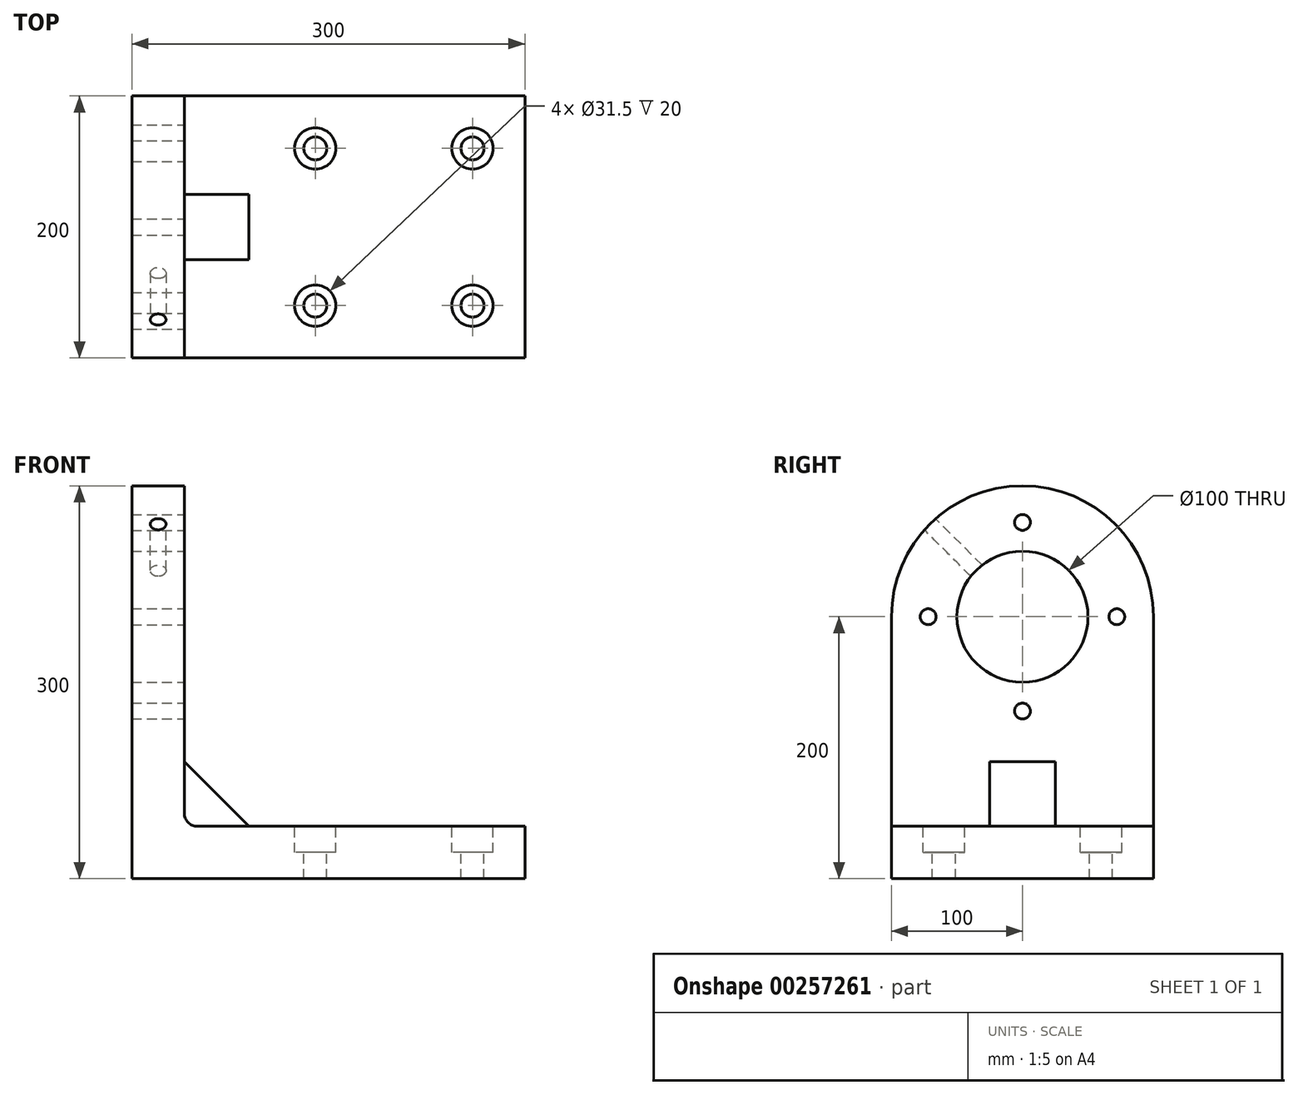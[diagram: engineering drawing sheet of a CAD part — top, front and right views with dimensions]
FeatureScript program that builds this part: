
annotation { "Feature Type Name" : "Feature", "Feature Type Description" : "" }
export const myFeature = defineFeature(function(context is Context, id is Id, definition is map)
    precondition{}
    {
        {
            var Q0;
            Q0=qCreatedBy(makeId("Front.planeOp"),FACE);
            var sketch = newSketch(context, id + "F0", { "sketchPlane" : qUnion([Q0])});
            skLineSegment(sketch, "E0", {"start": v(227.77, 0) * mm, "end": v(-72.23, 0) * mm});
            skLineSegment(sketch, "E1", {"start": v(-72.23, 0) * mm, "end": v(-72.23, 300) * mm});
            skLineSegment(sketch, "E2", {"start": v(-72.23, 300) * mm, "end": v(-32.23, 300) * mm});
            skLineSegment(sketch, "E3", {"start": v(-32.23, 300) * mm, "end": v(-32.23, 40) * mm});
            skLineSegment(sketch, "E4", {"start": v(-32.23, 40) * mm, "end": v(227.77, 40) * mm});
            skLineSegment(sketch, "E5", {"start": v(227.77, 40) * mm, "end": v(227.77, 0) * mm});
            skSolve(sketch);
        }
        {
            var Q0;
            Q0=makeQuery(id+"F0.imprint","IMPRINT",FACE,{"disambiguationData":[TD([[makeQuery(id+"F0.imprint","IMPRINT",EDGE,{"derivedFrom":sQuery(id+"F0.wireOp",EDGE,"E0")}),-1.0]])]});
            extrude(context, id + "F1", {"entities" : qUnion([Q0]), "endBound" : BoundingType.SYMMETRIC, "depth" : 200 * mm});
        }
        {
            var Q0;
            Q0=makeQuery(id+"F1.opExtrude","CAP_EDGE",EDGE,{"disambiguationData":[OSD([sQuery(id+"F0.wireOp",EDGE,"E2")])],"isStart":false});
            var Q1;
            Q1=makeQuery(id+"F1.opExtrude","CAP_EDGE",EDGE,{"disambiguationData":[OSD([sQuery(id+"F0.wireOp",EDGE,"E2")])],"isStart":true});
            fillet(context, id + "F2", {"entities" : qUnion([Q0, Q1]), "radius" : 100 * mm, "tangentPropagation" : true, "allowEdgeOverflow" : false});
        }
        {
            var Q0;
            Q0=makeQuery(id+"F1.opExtrude","SWEPT_FACE",FACE,{"disambiguationData":[OSD([sQuery(id+"F0.wireOp",EDGE,"E4")])]});
            var sketch = newSketch(context, id + "F3", { "sketchPlane" : qUnion([Q0])});
            skCircle(sketch, "E6", {"center": v(187.77, 60) * mm, "radius": 8.75 * mm});
            skCircle(sketch, "E7", {"center": v(67.77, 60) * mm, "radius": 8.75 * mm});
            skCircle(sketch, "E8", {"center": v(67.77, -60) * mm, "radius": 8.75 * mm});
            skCircle(sketch, "E9", {"center": v(187.77, -60) * mm, "radius": 8.75 * mm});
            skCircle(sketch, "E10", {"center": v(67.77, 60) * mm, "radius": 15.75 * mm});
            skCircle(sketch, "E11", {"center": v(187.77, 60) * mm, "radius": 15.75 * mm});
            skCircle(sketch, "E12", {"center": v(187.77, -60) * mm, "radius": 15.75 * mm});
            skCircle(sketch, "E13", {"center": v(67.77, -60) * mm, "radius": 15.75 * mm});
            skSolve(sketch);
        }
        {
            var Q0;
            Q0=makeQuery(id+"F3.imprint","IMPRINT",FACE,{"disambiguationData":[TD([[makeQuery(id+"F3.imprint","IMPRINT",EDGE,{"derivedFrom":sQuery(id+"F3.wireOp",EDGE,"E7")}),1.0]])]});
            var Q1;
            Q1=makeQuery(id+"F3.imprint","IMPRINT",FACE,{"disambiguationData":[TD([[makeQuery(id+"F3.imprint","IMPRINT",EDGE,{"derivedFrom":sQuery(id+"F3.wireOp",EDGE,"E6")}),1.0]])]});
            var Q2;
            Q2=makeQuery(id+"F3.imprint","IMPRINT",FACE,{"disambiguationData":[TD([[makeQuery(id+"F3.imprint","IMPRINT",EDGE,{"derivedFrom":sQuery(id+"F3.wireOp",EDGE,"E8")}),1.0]])]});
            var Q3;
            Q3=makeQuery(id+"F3.imprint","IMPRINT",FACE,{"disambiguationData":[TD([[makeQuery(id+"F3.imprint","IMPRINT",EDGE,{"derivedFrom":sQuery(id+"F3.wireOp",EDGE,"E9")}),1.0]])]});
            extrude(context, id + "F4", {"entities" : qUnion([Q0, Q1, Q2, Q3]), "operationType" : NewBodyOperationType.REMOVE, "endBound" : BoundingType.THROUGH_ALL, "oppositeDirection" : true, "depth" : 25.4 * mm});
        }
        {
            var Q0;
            Q0=makeQuery(id+"F3.imprint","IMPRINT",FACE,{"disambiguationData":[TD([[makeQuery(id+"F3.imprint","IMPRINT",EDGE,{"derivedFrom":sQuery(id+"F3.wireOp",EDGE,"E6")}),-1.0]])]});
            var Q1;
            Q1=makeQuery(id+"F3.imprint","IMPRINT",FACE,{"disambiguationData":[TD([[makeQuery(id+"F3.imprint","IMPRINT",EDGE,{"derivedFrom":sQuery(id+"F3.wireOp",EDGE,"E7")}),-1.0]])]});
            var Q2;
            Q2=makeQuery(id+"F3.imprint","IMPRINT",FACE,{"disambiguationData":[TD([[makeQuery(id+"F3.imprint","IMPRINT",EDGE,{"derivedFrom":sQuery(id+"F3.wireOp",EDGE,"E8")}),-1.0]])]});
            var Q3;
            Q3=makeQuery(id+"F3.imprint","IMPRINT",FACE,{"disambiguationData":[TD([[makeQuery(id+"F3.imprint","IMPRINT",EDGE,{"derivedFrom":sQuery(id+"F3.wireOp",EDGE,"E9")}),-1.0]])]});
            extrude(context, id + "F5", {"entities" : qUnion([Q0, Q1, Q2, Q3]), "operationType" : NewBodyOperationType.REMOVE, "oppositeDirection" : true, "depth" : 20 * mm});
        }
        {
            var Q0;
            Q0=makeQuery(id+"F1.opExtrude","SWEPT_FACE",FACE,{"disambiguationData":[OSD([sQuery(id+"F0.wireOp",EDGE,"E3")])]});
            var sketch = newSketch(context, id + "F6", { "sketchPlane" : qUnion([Q0])});
            skCircle(sketch, "E14", {"center": v(0, 200) * mm, "radius": 50 * mm});
            skSolve(sketch);
        }
        {
            var Q0;
            Q0=makeQuery(id+"F6.imprint","IMPRINT",FACE,{"disambiguationData":[TD([[makeQuery(id+"F6.imprint","IMPRINT",EDGE,{"derivedFrom":sQuery(id+"F6.wireOp",EDGE,"E14")}),1.0]])]});
            extrude(context, id + "F7", {"entities" : qUnion([Q0]), "operationType" : NewBodyOperationType.REMOVE, "endBound" : BoundingType.THROUGH_ALL, "oppositeDirection" : true, "depth" : 25.4 * mm});
        }
        {
            var Q0;
            Q0=makeQuery(id+"F6.imprint","IMPRINT",FACE,{"disambiguationData":[TD([[makeQuery(id+"F6.imprint","IMPRINT",EDGE,{"derivedFrom":sQuery(id+"F6.wireOp",EDGE,"E14")}),-1.0]])]});
            var sketch = newSketch(context, id + "F8", { "sketchPlane" : qUnion([Q0])});
            skCircle(sketch, "E15", {"center": v(0, 200) * mm, "radius": 72 * mm, "construction": true});
            skPoint(sketch, "E16", {"position": v(72, 200) * mm});
            skPoint(sketch, "E17", {"position": v(0, 272) * mm});
            skPoint(sketch, "E18", {"position": v(-72, 200) * mm});
            skPoint(sketch, "E19", {"position": v(0, 128) * mm});
            skLineSegment(sketch, "E20", {"start": v(0, 200) * mm, "end": v(-70.71, 270.71) * mm, "construction": true});
            skLineSegment(sketch, "E21", {"start": v(0, 200) * mm, "end": v(0, 272) * mm, "construction": true});
            skSolve(sketch);
        }
        {
            var Q0;
            Q0=makeQuery(id+"F1.opExtrude","CAP_FACE",FACE,{"disambiguationData":[OSD([sQuery(id+"F0.wireOp",EDGE,"E0"),sQuery(id+"F0.wireOp",EDGE,"E1"),sQuery(id+"F0.wireOp",EDGE,"E2"),sQuery(id+"F0.wireOp",EDGE,"E3"),sQuery(id+"F0.wireOp",EDGE,"E4"),sQuery(id+"F0.wireOp",EDGE,"E5")])],"isStart":true});
            cPlane(context, id + "F9", {"entities" : qUnion([Q0]), "cplaneType" : CPlaneType.OFFSET, "offset" : 100 * mm, "oppositeDirection" : true, "width" : 152.4 * mm, "height" : 152.4 * mm});
        }
        {
            var Q0;
            Q0=qCreatedBy(id+"F9.planeOp",FACE);
            var sketch = newSketch(context, id + "F10", { "sketchPlane" : qUnion([Q0])});
            skLineSegment(sketch, "E22.0", {"start": v(32.23, 40) * mm, "end": v(-227.77, 40) * mm});
            skLineSegment(sketch, "E23.0", {"start": v(32.23, 200) * mm, "end": v(32.23, 40) * mm});
            skLineSegment(sketch, "E24", {"start": v(-17.15, 40) * mm, "end": v(32.23, 89.38) * mm});
            skSolve(sketch);
        }
        {
            var Q0;
            Q0 = qSketchRegion(id + "F10", true);
            extrude(context, id + "F11", {"entities" : qUnion([Q0]), "operationType" : NewBodyOperationType.ADD, "endBound" : BoundingType.SYMMETRIC, "depth" : 50 * mm});
        }
        {
            var Q0;
            {var subQ0=sQuery(id+"F0.wireOp",EDGE,"E4");var subQ1=sQuery(id+"F0.wireOp",EDGE,"E3");Q0=makeQuery(id+"F11.boolean.opBoolean","SPLIT",EDGE,{"disambiguationData":[TD([makeQuery(id+"F11.opExtrude","CAP_FACE",FACE,{"disambiguationData":[OSD([sQuery(id+"F10.wireOp",EDGE,"E22.0"),sQuery(id+"F10.wireOp",EDGE,"E23.0"),sQuery(id+"F10.wireOp",EDGE,"E24")])],"isStart":false})])],"derivedFrom":makeQuery(id+"F1.opExtrude","SWEPT_EDGE",EDGE,{"disambiguationData":[OSD([subQ1,subQ0])]})});}
            var Q1;
            {var subQ0=sQuery(id+"F0.wireOp",EDGE,"E4");var subQ1=sQuery(id+"F0.wireOp",EDGE,"E3");Q1=makeQuery(id+"F11.boolean.opBoolean","SPLIT",EDGE,{"disambiguationData":[TD([makeQuery(id+"F11.opExtrude","CAP_FACE",FACE,{"disambiguationData":[OSD([sQuery(id+"F10.wireOp",EDGE,"E22.0"),sQuery(id+"F10.wireOp",EDGE,"E23.0"),sQuery(id+"F10.wireOp",EDGE,"E24")])],"isStart":true})])],"derivedFrom":makeQuery(id+"F1.opExtrude","SWEPT_EDGE",EDGE,{"disambiguationData":[OSD([subQ1,subQ0])]})});}
            fillet(context, id + "F12", {"entities" : qUnion([Q0, Q1]), "radius" : 10 * mm, "tangentPropagation" : true, "allowEdgeOverflow" : false});
        }
        {
            var Q0;
            Q0=sQuery(id+"F8.wireOp",VERTEX,"E17");
            var Q1;
            Q1=sQuery(id+"F8.wireOp",VERTEX,"E16");
            var Q2;
            Q2=sQuery(id+"F8.wireOp",VERTEX,"E19");
            var Q3;
            Q3=sQuery(id+"F8.wireOp",VERTEX,"E18");
            var Q4;
            Q4=makeQuery(id+"F1.opExtrude","SWEPT_BODY",BODY,{"disambiguationData":[OSD([sQuery(id+"F0.wireOp",EDGE,"E0"),sQuery(id+"F0.wireOp",EDGE,"E1"),sQuery(id+"F0.wireOp",EDGE,"E2"),sQuery(id+"F0.wireOp",EDGE,"E3"),sQuery(id+"F0.wireOp",EDGE,"E4"),sQuery(id+"F0.wireOp",EDGE,"E5")])]});
            hole(context, id + "F13", {"style" : HoleStyle.SIMPLE, "endStyle" : HoleEndStyle.THROUGH, "standardTappedOrClearance" : lookupTablePath({ "standard" : "ISO", "engagement" : "75%", "pitch" : "2 mm", "size" : "M14", "type" : "Tapped" }), "standardBlindInLast" : lookupTablePath({ "standard" : "ISO", "engagement" : "75%", "pitch" : "2 mm", "size" : "M14", "type" : "Tapped" }), "holeDiameter" : 12.1 * mm, "showTappedDepth" : true, "tappedDepth" : 12.7 * mm, "tapClearance" : 3, "locations" : qUnion([Q0, Q1, Q2, Q3]), "scope" : qUnion([Q4]), "majorDiameter" : 14 * mm});
        }
        {
            var Q0;
            Q0=sQuery(id+"F8.wireOp",EDGE,"E20");
            var Q1;
            Q1=sQuery(id+"F8.wireOp",VERTEX,"E20.end");
            cPlane(context, id + "F14", {"entities" : qUnion([Q0, Q1]), "cplaneType" : CPlaneType.LINE_POINT, "offset" : 25.4 * mm, "width" : 152.4 * mm, "height" : 152.4 * mm});
        }
        {
            var Q0;
            Q0=qCreatedBy(id+"F14.planeOp",FACE);
            var sketch = newSketch(context, id + "F15", { "sketchPlane" : qUnion([Q0])});
            skPoint(sketch, "E25.0", {"position": v(-32.23, 141.42) * mm});
            skLineSegment(sketch, "E26", {"start": v(-32.23, 141.42) * mm, "end": v(-72.23, 141.42) * mm, "construction": true});
            skPoint(sketch, "E27", {"position": v(-52.23, 141.42) * mm});
            skSolve(sketch);
        }
        {
            var Q0;
            Q0=sQuery(id+"F15.wireOp",VERTEX,"E27");
            var Q1;
            Q1=makeQuery(id+"F1.opExtrude","SWEPT_BODY",BODY,{"disambiguationData":[OSD([sQuery(id+"F0.wireOp",EDGE,"E0"),sQuery(id+"F0.wireOp",EDGE,"E1"),sQuery(id+"F0.wireOp",EDGE,"E2"),sQuery(id+"F0.wireOp",EDGE,"E3"),sQuery(id+"F0.wireOp",EDGE,"E4"),sQuery(id+"F0.wireOp",EDGE,"E5")])]});
            hole(context, id + "F16", {"style" : HoleStyle.SIMPLE, "endStyle" : HoleEndStyle.BLIND, "standardTappedOrClearance" : lookupTablePath({ "standard" : "ISO", "engagement" : "75%", "pitch" : "2 mm", "size" : "M14", "type" : "Tapped" }), "standardBlindInLast" : lookupTablePath({ "standard" : "ISO", "engagement" : "75%", "pitch" : "2 mm", "size" : "M14", "type" : "Tapped" }), "holeDiameter" : 12.1 * mm, "showTappedDepth" : true, "holeDepth" : 69.85 * mm, "tappedDepth" : 63.85 * mm, "tapClearance" : 3, "locations" : qUnion([Q0]), "scope" : qUnion([Q1]), "majorDiameter" : 14 * mm});
        }
    });
